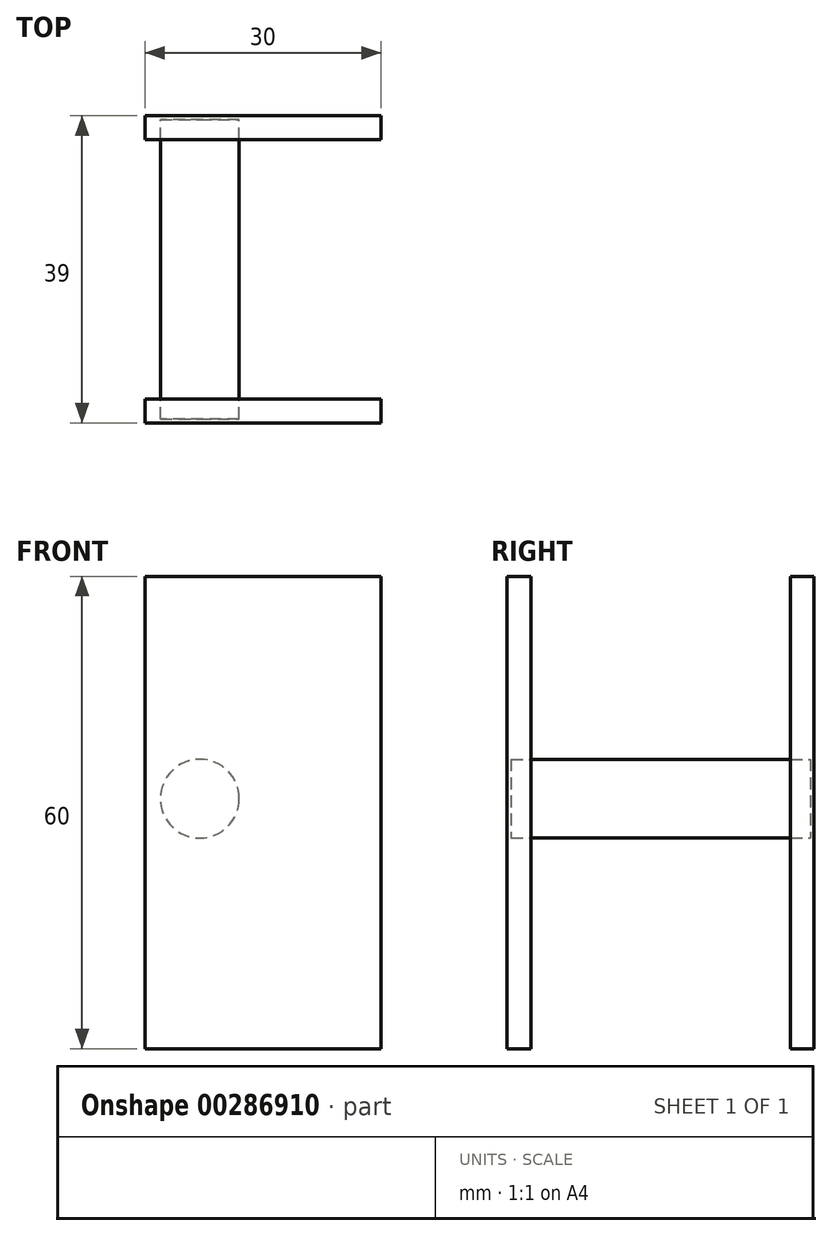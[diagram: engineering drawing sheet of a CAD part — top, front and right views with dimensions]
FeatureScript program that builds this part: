
annotation { "Feature Type Name" : "Feature", "Feature Type Description" : "" }
export const myFeature = defineFeature(function(context is Context, id is Id, definition is map)
    precondition{}
    {
        {
            var Q0;
            Q0=qCreatedBy(makeId("Front.planeOp"),FACE);
            var sketch = newSketch(context, id + "F0", { "sketchPlane" : qUnion([Q0])});
            skLineSegment(sketch, "E0.bottom", {"start": v(-15.75, 28.24) * mm, "end": v(14.25, 28.24) * mm});
            skLineSegment(sketch, "E0.top", {"start": v(-15.75, -31.76) * mm, "end": v(14.25, -31.76) * mm});
            skLineSegment(sketch, "E0.left", {"start": v(-15.75, 28.24) * mm, "end": v(-15.75, -31.76) * mm});
            skLineSegment(sketch, "E0.right", {"start": v(14.25, 28.24) * mm, "end": v(14.25, -31.76) * mm});
            skSolve(sketch);
        }
        {
            var Q0;
            Q0 = qSketchRegion(id + "F0", true);
            extrude(context, id + "F1", {"entities" : qUnion([Q0]), "depth" : 3 * mm});
        }
        {
            var Q0;
            Q0=makeQuery(id+"F1.opExtrude","SWEPT_BODY",BODY,{"disambiguationData":[OSD([sQuery(id+"F0.wireOp",EDGE,"E0.bottom"),sQuery(id+"F0.wireOp",EDGE,"E0.top"),sQuery(id+"F0.wireOp",EDGE,"E0.left"),sQuery(id+"F0.wireOp",EDGE,"E0.right")])]});
            var Q1;
            Q1=makeQuery(id+"F1.opExtrude","CAP_FACE",FACE,{"disambiguationData":[OSD([sQuery(id+"F0.wireOp",EDGE,"E0.bottom"),sQuery(id+"F0.wireOp",EDGE,"E0.top"),sQuery(id+"F0.wireOp",EDGE,"E0.left"),sQuery(id+"F0.wireOp",EDGE,"E0.right")])],"isStart":false});
            mirror(context, id + "F2", {"entities" : qUnion([Q0]), "mirrorPlane" : qUnion([Q1])});
        }
        {
            var Q0;
            Q0=makeQuery(id+"F2.opPattern","COPY",BODY,{"derivedFrom":makeQuery(id+"F1.opExtrude","SWEPT_BODY",BODY,{"disambiguationData":[OSD([sQuery(id+"F0.wireOp",EDGE,"E0.bottom"),sQuery(id+"F0.wireOp",EDGE,"E0.top"),sQuery(id+"F0.wireOp",EDGE,"E0.left"),sQuery(id+"F0.wireOp",EDGE,"E0.right")])]}),"instanceName":"1"});
            transform(context, id + "F3", {"entities" : qUnion([Q0]), "transformType" : TransformType.TRANSLATION_3D, "dx" : 0 * mm, "dy" : -33 * mm, "dz" : 0 * mm, "makeCopy" : false});
        }
        {
            var Q0;
            Q0=makeQuery(id+"F1.opExtrude","CAP_FACE",FACE,{"disambiguationData":[OSD([sQuery(id+"F0.wireOp",EDGE,"E0.bottom"),sQuery(id+"F0.wireOp",EDGE,"E0.top"),sQuery(id+"F0.wireOp",EDGE,"E0.left"),sQuery(id+"F0.wireOp",EDGE,"E0.right")])],"isStart":true});
            var sketch = newSketch(context, id + "F4", { "sketchPlane" : qUnion([Q0])});
            skCircle(sketch, "E1", {"center": v(8.78, 0) * mm, "radius": 5 * mm});
            skSolve(sketch);
        }
        {
            var Q0;
            Q0=makeQuery(id+"F4.imprint","IMPRINT",FACE,{"disambiguationData":[TD([[makeQuery(id+"F4.imprint","IMPRINT",EDGE,{"derivedFrom":sQuery(id+"F4.wireOp",EDGE,"E1")}),1.0]])]});
            extrude(context, id + "F5", {"entities" : qUnion([Q0]), "oppositeDirection" : true, "depth" : 38 * mm});
        }
        {
            var Q0;
            Q0=makeQuery(id+"F5.opExtrude","SWEPT_BODY",BODY,{"disambiguationData":[OSD([sQuery(id+"F4.wireOp",EDGE,"E1")])]});
            transform(context, id + "F6", {"entities" : qUnion([Q0]), "transformType" : TransformType.TRANSLATION_3D, "dx" : 0 * mm, "dy" : -0.5 * mm, "dz" : 0 * mm, "makeCopy" : false});
        }
    });
